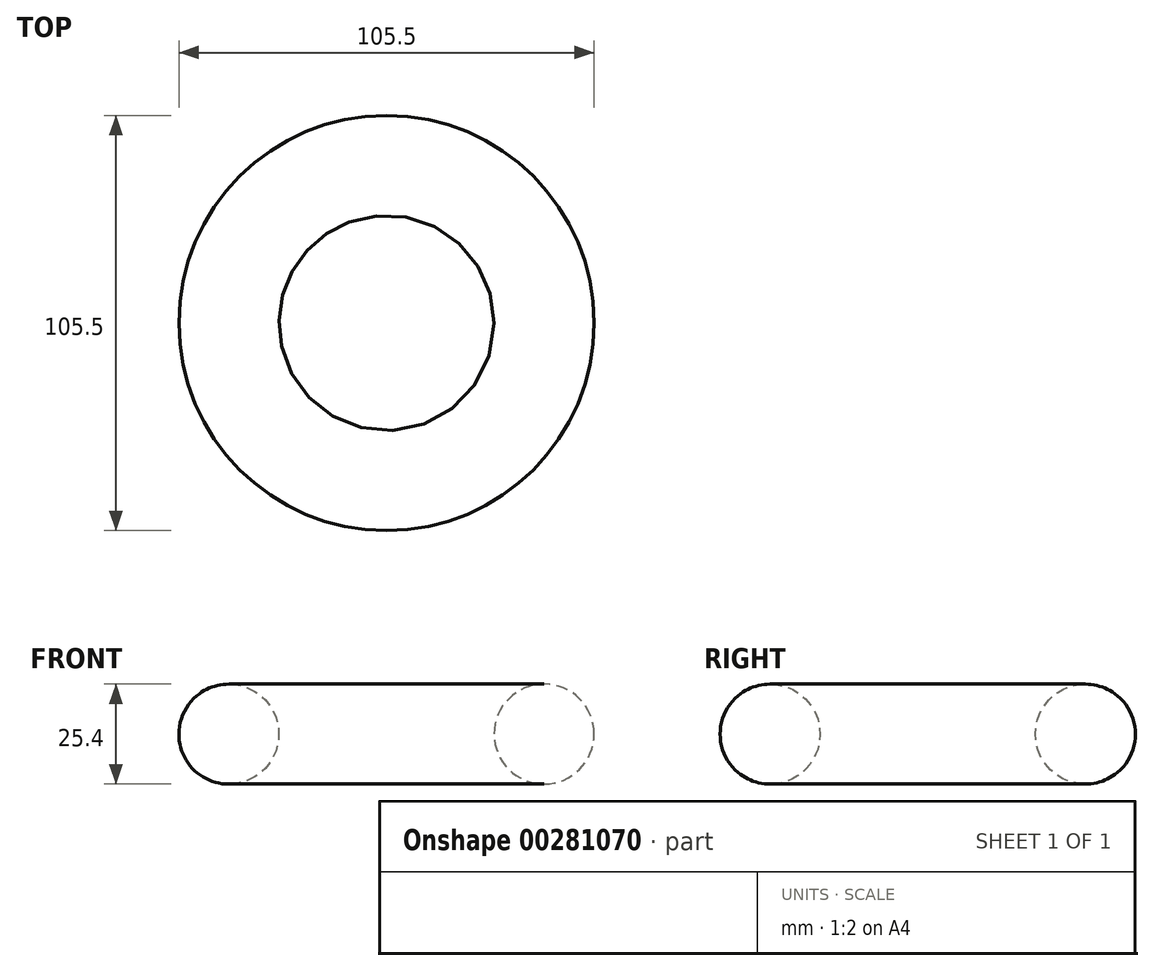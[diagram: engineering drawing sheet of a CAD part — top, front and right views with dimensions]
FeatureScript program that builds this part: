
annotation { "Feature Type Name" : "Feature", "Feature Type Description" : "" }
export const myFeature = defineFeature(function(context is Context, id is Id, definition is map)
    precondition{}
    {
        {
            var Q0;
            Q0=qCreatedBy(makeId("Front.planeOp"),FACE);
            var sketch = newSketch(context, id + "F0", { "sketchPlane" : qUnion([Q0])});
            skLineSegment(sketch, "E0", {"start": v(0, 0) * mm, "end": v(0, 76) * mm, "construction": true});
            skLineSegment(sketch, "E1", {"start": v(0, 76) * mm, "end": v(0, -76.4) * mm, "construction": true});
            skCircle(sketch, "E2", {"center": v(-40.05, 0) * mm, "radius": 12.7 * mm});
            skSolve(sketch);
        }
        {
            var Q0;
            Q0=makeQuery(id+"F0.imprint","IMPRINT",FACE,{"disambiguationData":[TD([[makeQuery(id+"F0.imprint","IMPRINT",EDGE,{"derivedFrom":sQuery(id+"F0.wireOp",EDGE,"E2")}),1.0]])]});
            var Q1;
            Q1=sQuery(id+"F0.wireOp",EDGE,"E1");
            revolve(context, id + "F1", {"entities" : qUnion([Q0]), "axis" : qUnion([Q1]), "revolveType" : RevolveType.FULL});
        }
    });
